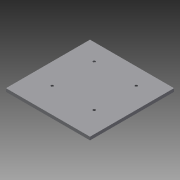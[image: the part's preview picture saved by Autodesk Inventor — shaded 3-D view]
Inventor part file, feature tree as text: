
AUTODESK INVENTOR PART (.ipt)
format: ipt  version: 2013 (Build 170138000, 138)  size: 89,088 bytes
history: native  units: in
note: dims shown in document units (in); Inventor stores cm internally (conversion verified against a paired STEP export)
features: extrude x1, hole x1, sketch x1
ambient origin geometry x8: Origin, YZ Plane, XZ Plane, XY Plane, X Axis, Y Axis, Z Axis, Center Point
bodies: Solid1 (feature_tree)
feature tree (3):
  extrude  "Extrusion1"  Depth=5.0in
  hole  "Hole1"  [1 undecoded]
  sketch  "Sketch2"  dims[d0=5.0in d1=5.0in d2=0.1875in d3=0.0in d4=2.5in d6=1.25in d8=1.25in d9=2.5in d10=1.0in d11=0.145in d12=0.75in d13=0.375in d14=0.25in d15=0.5635in d16=1.0in d17=0.8108in]
note: 1 required parameter value undecoded (feature->parameter linkage not recoverable at this tier; creation-order binding heuristic only, values carry confidence <= 0.55)
